# Revit family: Faucet-Kitchen-KOHLER-Bellera-K-560
name_source: partatom
category: Plumbing Fixtures
revit_build: Autodesk Revit 2015 (Build: 20140606_1530(x64)
units: mm (PartAtom-declared; Revit-internal decimal feet)

## types (3) — shared parameters
ADA Compliant = Yes
Assembly Code = D2010
CW Connection = Yes
Cold Water Inlet = Cold Water Inlet
Date Modified = 01/11/2019
Default Elevation = 36"
Description = Single-hole or three-hole kitchen sink faucet with pull-down 16-3/4 inch spout and right-hand lever handle, DockNetik magnetic docking system, and a 3-function sprayhead featuring Sweep spray
Drain Included = No
Flow Rate = 2 GPM
HW Connection = Yes
Hot Water Inlet = Hot Water Inlet
Length = 7 7/8"
Manufacturer = KOHLER Co.
MasterFormat 1995 = 15410
MasterFormat 2004 = 22.41.39
Material = Premium Metal Construction
Pressure = 60.00 psi
Product Documentation Link = http://www.us.kohler.com
Product Name = Bellera
Product Page URL = http://www.us.kohler.com
Spout Reach = 7 7/8"
URL = https://www.us.kohler.com
Vent Connection = No
Waste Connection = No
Waste Water Outlet = Waste Water Outlet

## per-type parameters (varying)
| type | Finish | Model | Type |
| CP-Polished Chrome | Kohler-Metal-CP-Polished_Chrome | K-560-CP | 1 |
| VS-Vibrant Stainless | Kohler-Metal-VS-Vibrant_Stainless | K-560-VS | 2 |
| 2BZ-Oil-Rubbed Bronze | Kohler-Metal-2BZ-Oil_Rubbed_Bronze | K-560-2BZ | 3 |

## geometry (parser evidence)
native form markers: Sweep x19
no freeform markers — native parametric forms only
